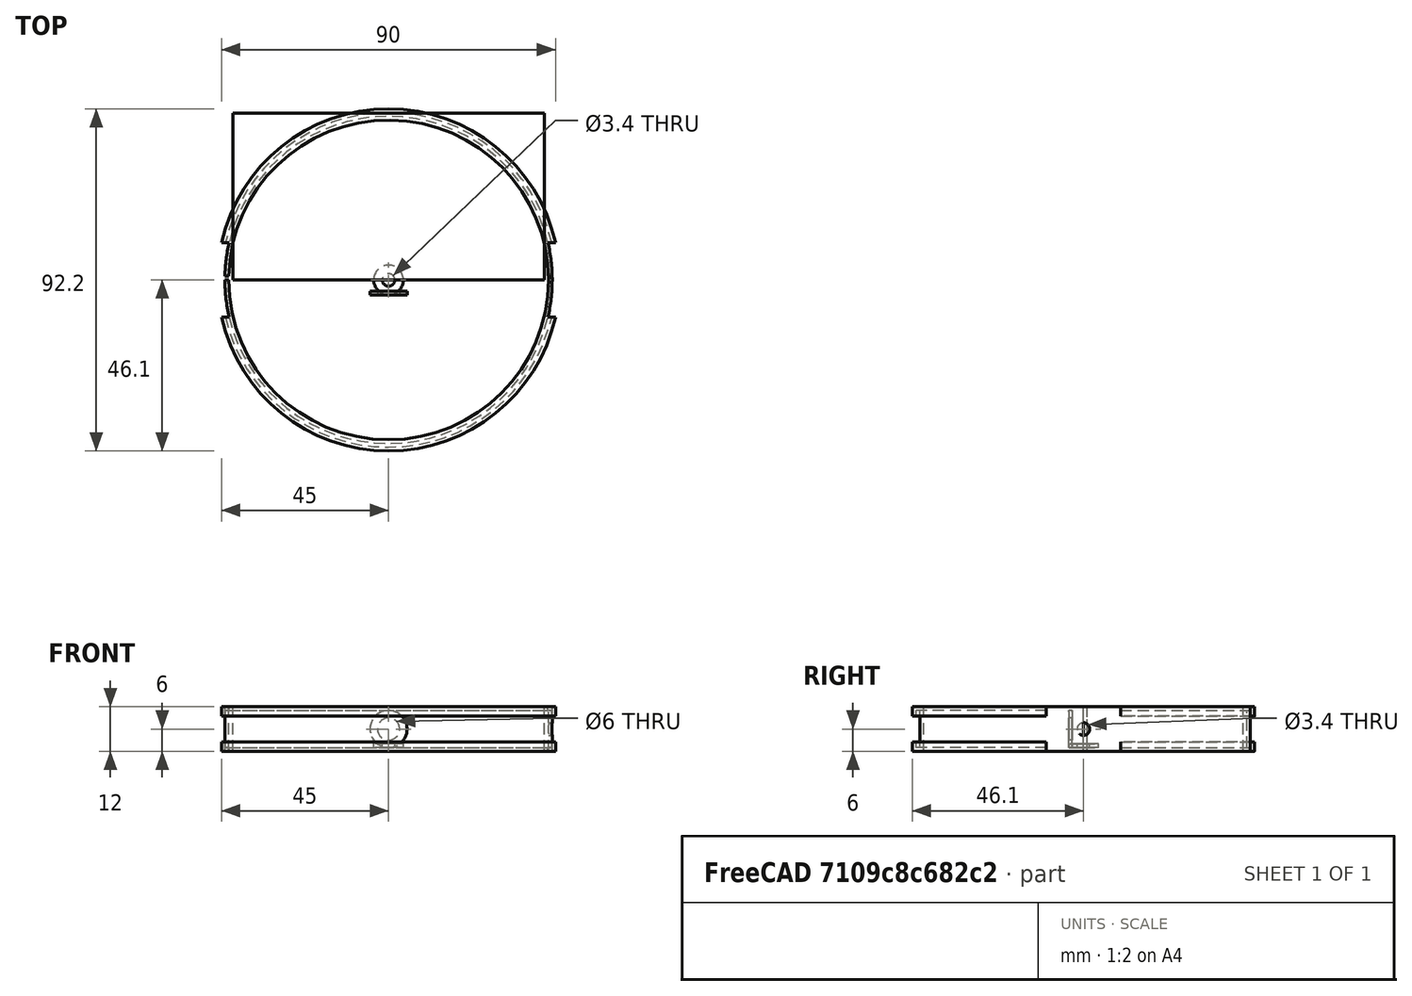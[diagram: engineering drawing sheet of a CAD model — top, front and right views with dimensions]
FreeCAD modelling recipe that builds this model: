
FCSTD DOCUMENT  (FreeCAD 0.18R16131 (Git))
Label: led_bauble_8led
License: All rights reserved
LicenseURL: http://en.wikipedia.org/wiki/All_rights_reserved
objects: Part::Cylinder×13, Part::Cut×13, Part::Box×4
note: 30 computed .brp shape members not serialized (recipe doc carries the construction recipe); baked Part::Feature solids carry a one-line shape summary decoded from their .brp

FEATURE [Part::Cylinder] Cylinder001  label="Cylinder(led_gap)(radius_plus_two)"
  Angle = 360
  AttacherType = Attacher::AttachEngine3D
  Height = 7
  Placement = pos=(0,0,1.5) rot=(0,0,1;0rad)
  Radius = 46.1
FEATURE [Part::Cylinder] Cylinder002  label="Cylinder(outer)(radius_plus_two)"
  Angle = 360
  AttacherType = Attacher::AttachEngine3D
  Height = 12
  Placement = pos=(0,0,-1) rot=(0,0,1;0rad)
  Radius = 46.1
FEATURE [Part::Cylinder] Cylinder003  label="Cylinder(outer_cut)(radius_take_one)"
  Angle = 360
  AttacherType = Attacher::AttachEngine3D
  Height = 12
  Placement = pos=(0,0,-1) rot=(0,0,1;0rad)
  Radius = 43.1
FEATURE [Part::Cylinder] Cylinder004  label="Cylinder(inner_cut)(radius)"
  Angle = 360
  AttacherType = Attacher::AttachEngine3D
  Height = 10
  Radius = 44.1
FEATURE [Part::Cylinder] Cylinder005  label="Cylinder(led_gap_cut)(radius_plus_one)"
  Angle = 360
  AttacherType = Attacher::AttachEngine3D
  Height = 7
  Placement = pos=(0,0,1.5) rot=(0,0,1;0rad)
  Radius = 45.1
FEATURE [Part::Box] Box003  label="Cube"
  AttacherType = Attacher::AttachEngine3D
  Height = 12
  Length = 90
  Placement = pos=(-45,10,-1) rot=(0,0,1;0rad)
  Width = 40
FEATURE [Part::Cylinder] Cylinder  label="Cylinder(inner)(radius_plus_one)"
  Angle = 360
  AttacherType = Attacher::AttachEngine3D
  Height = 10
  Radius = 45.1
FEATURE [Part::Cylinder] Cylinder006  label="Cylinder(outer_channel_cut)(radius_plue_two)"
  Angle = 360
  AttacherType = Attacher::AttachEngine3D
  Height = 12
  Placement = pos=(0,0,-1) rot=(0,0,1;0rad)
  Radius = 46.1
FEATURE [Part::Cylinder] Cylinder007  label="Cylinder001(inner_channel_cut)(radius)"
  Angle = 360
  AttacherType = Attacher::AttachEngine3D
  Height = 12
  Placement = pos=(0,0,-1) rot=(0,0,1;0rad)
  Radius = 44.1
FEATURE [Part::Box] Box004  label="Cube001"
  AttacherType = Attacher::AttachEngine3D
  Height = 12
  Length = 90
  Placement = pos=(-45,-50,-1) rot=(0,0,1;0rad)
  Width = 40
FEATURE [Part::Cylinder] Cylinder008  label="Cylinder(m3_hole)"
  Angle = 360
  AttacherType = Attacher::AttachEngine3D
  Height = 10
  Placement = pos=(35,0,5) rot=(0,1,0;1.5708rad)
  Radius = 1.7
FEATURE [Part::Box] Box005  label="Cube002"
  AttacherType = Attacher::AttachEngine3D
  Height = 12
  Length = 84
  Placement = pos=(-42,0,-1) rot=(0,0,1;0rad)
  Width = 45
FEATURE [Part::Box] Box  label="Cube003"
  AttacherType = Attacher::AttachEngine3D
  Height = 12
  Length = 5
  Placement = pos=(-45,0,-1) rot=(0,0,1;0rad)
  Width = 1
FEATURE [Part::Cut] Cut
  Base = -> Cylinder
  Tool = -> Cylinder004
FEATURE [Part::Cut] Cut001
  Base = -> Cylinder002
  Tool = -> Cylinder003
FEATURE [Part::Cut] Cut002
  Base = -> Cylinder001
  Tool = -> Cylinder005
FEATURE [Part::Cut] Cut003
  Base = -> Cut001
  Tool = -> Cut
FEATURE [Part::Cut] Cut004
  Base = -> Cut003
  Tool = -> Cut002
FEATURE [Part::Cut] Cut005
  Base = -> Cylinder006
  Tool = -> Cylinder007
FEATURE [Part::Cut] Cut006
  Base = -> Cut005
  Tool = -> Box004
FEATURE [Part::Cut] Cut007
  Base = -> Cut006
  Tool = -> Box003
FEATURE [Part::Cut] Cut008
  Base = -> Cut004
  Tool = -> Cut007
FEATURE [Part::Cut] Cut009
  Base = -> Cut008
  Tool = -> Box
FEATURE [Part::Cut] Cut010
  Base = -> Cut009
  Tool = -> Cylinder008
FEATURE [Part::Cylinder] Cylinder009  label="Cylinder(m3_cut)"
  Angle = 360
  AttacherType = Attacher::AttachEngine3D
  Height = 1
  Radius = 1.7
FEATURE [Part::Cylinder] Cylinder010  label="Cylinder001(washer_base)"
  Angle = 360
  AttacherType = Attacher::AttachEngine3D
  Height = 1
  Radius = 4
FEATURE [Part::Cylinder] Cylinder011  label="Cylinder001(washer_vertical_cut)"
  Angle = 360
  AttacherType = Attacher::AttachEngine3D
  Height = 1
  Placement = pos=(0,-3,5) rot=(1,0,0;1.5708rad)
  Radius = 3
FEATURE [Part::Cut] Cut011
  Base = -> Cylinder010
  Tool = -> Cylinder009
FEATURE [Part::Cylinder] Cylinder012  label="Cylinder001(washer_vertical)"
  Angle = 360
  AttacherType = Attacher::AttachEngine3D
  Height = 1
  Placement = pos=(0,-3,5) rot=(1,0,0;1.5708rad)
  Radius = 5
FEATURE [Part::Cut] Cut012
  Base = -> Cylinder012
  Tool = -> Cylinder011
